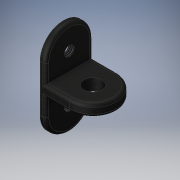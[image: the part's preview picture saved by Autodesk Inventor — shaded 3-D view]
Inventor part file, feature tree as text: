
AUTODESK INVENTOR PART (.ipt)
format: ipt  version: 2018 (Build 220112000, 112)  size: 173,056 bytes
history: native  units: in
note: dims shown in document units (in); Inventor stores cm internally (conversion verified against a paired STEP export)
features: fillet x2, hole x2, sketch x2, extrude x1
ambient origin geometry x8: Origin, YZ Plane, XZ Plane, XY Plane, X Axis, Y Axis, Z Axis, Center Point
bodies: Solid1 (feature_tree)
feature tree (7):
  extrude  "Extrusion1"  Depth=0.25in
  fillet  "Fillet1"  Radius=2.0in
  fillet  "Fillet2"  Radius=0.25in
  hole  "Hole1"  [1 undecoded]
  hole  "Hole2"  [1 undecoded]
  sketch  "Sketch1"  dims[d0=0.5in d1=4.0in d2=2.0in d3=0.25in]
  sketch  "Sketch2"  dims[d4=2.0in d5=0.0in d6=1.0in d7=0.125in d25=1.0in d26=1.0in d10=0.75in d11=0.75in d12=0.375in d13=0.25in d14=0.5635in d15=1.0in d16=0.8108in d17=2.0in d18=0.417in d19=1.0in d20=0.375in d21=0.25in d22=0.5635in d23=1.385in d24=0.8108in]
note: 2 required parameter values undecoded (feature->parameter linkage not recoverable at this tier; creation-order binding heuristic only, values carry confidence <= 0.55)
